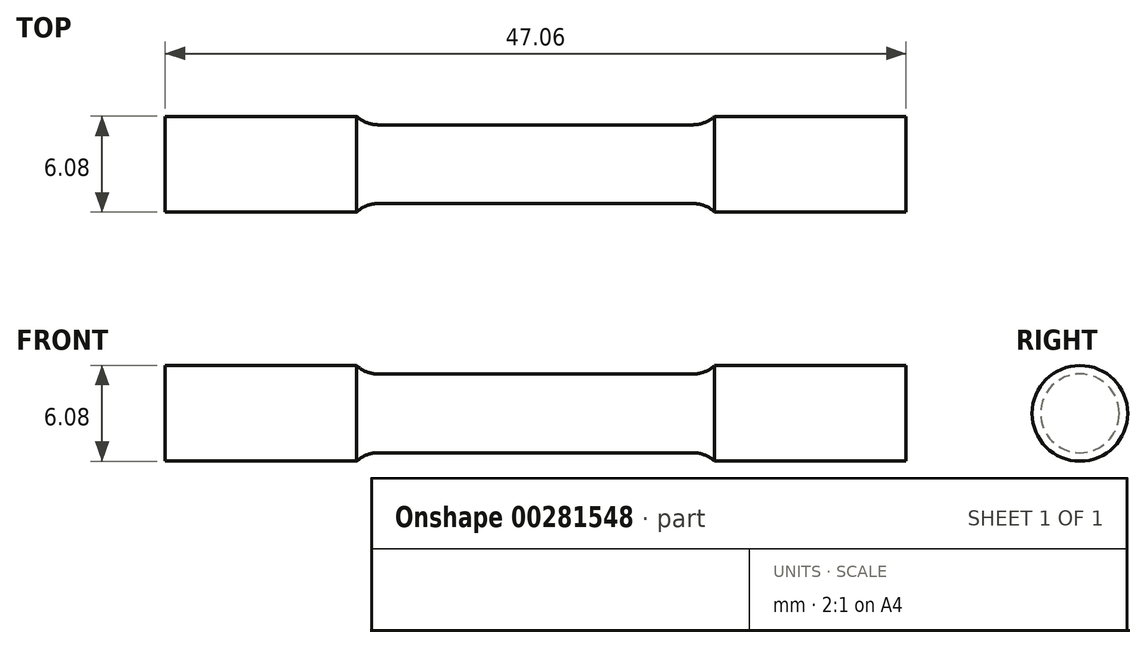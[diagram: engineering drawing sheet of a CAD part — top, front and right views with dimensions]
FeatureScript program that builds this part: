
annotation { "Feature Type Name" : "Feature", "Feature Type Description" : "" }
export const myFeature = defineFeature(function(context is Context, id is Id, definition is map)
    precondition{}
    {
        {
            var Q0;
            Q0=qCreatedBy(makeId("Front.planeOp"),FACE);
            var sketch = newSketch(context, id + "F0", { "sketchPlane" : qUnion([Q0])});
            skLineSegment(sketch, "E0", {"start": v(0, 2.5) * mm, "end": v(10, 2.5) * mm});
            skArc(sketch, "E1", {"start": v(10, 2.5) * mm, "mid": v(10.73, 2.64) * mm, "end": v(11.36, 3.04) * mm});
            skLineSegment(sketch, "E2", {"start": v(11.36, 3.04) * mm, "end": v(23.53, 3.04) * mm});
            skLineSegment(sketch, "E3", {"start": v(23.53, 3.04) * mm, "end": v(23.53, 0) * mm});
            skLineSegment(sketch, "E4.MirrorCS", {"start": v(0, 2.5) * mm, "end": v(-10, 2.5) * mm});
            skLineSegment(sketch, "E5.MirrorCS", {"start": v(-23.53, 3.04) * mm, "end": v(-23.53, 0) * mm});
            skLineSegment(sketch, "E6.MirrorCS", {"start": v(-11.36, 3.04) * mm, "end": v(-23.53, 3.04) * mm});
            skArc(sketch, "E7.MirrorCS", {"start": v(-10, 2.5) * mm, "mid": v(-10.73, 2.64) * mm, "end": v(-11.36, 3.04) * mm});
            skLineSegment(sketch, "E8", {"start": v(-23.53, 0) * mm, "end": v(23.53, 0) * mm});
            skSolve(sketch);
        }
        {
            var Q0;
            Q0 = qSketchRegion(id + "F0", true);
            var Q1;
            Q1=sQuery(id+"F0.wireOp",EDGE,"E8");
            revolve(context, id + "F1", {"entities" : qUnion([Q0]), "axis" : qUnion([Q1]), "revolveType" : RevolveType.FULL});
        }
    });
